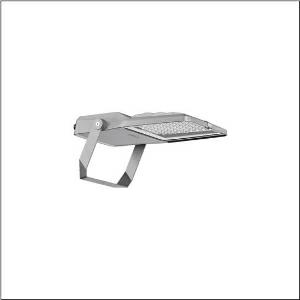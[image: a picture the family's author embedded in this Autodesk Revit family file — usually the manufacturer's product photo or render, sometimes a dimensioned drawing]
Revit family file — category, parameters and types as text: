
# Revit family: floodlight_fl_21_iq_mini___pl64_5xa7772c2e1a_df54
name_source: partatom
category: Lighting Fixtures
units: mm (PartAtom-declared; Revit-internal decimal feet)

## family parameters
Cut with Voids When Loaded = No
Host = Face
Light Source = No
Part Type = Normal
Room Calculation Point = No
Round Connector Dimension = Use Diameter
Shared = No

## types (1)
- --- (1 x LED, 11790 lm, 87.2 W, 3000K)
    Apparent Load = 87 VA
    CIE Flux Codes = 28 80 98 100 100
    Color Rendering = 70
    Color Temperature = 3000K
    Default Elevation = 1800 mm
    Description = Floodlight FL 21 iQ mini, floodlight, primary light control with lens, of PMMA, primary optical cover: protective disc, of toughened safety glass, transparent, light distribution: PL64, light emission: direct distribution, installation type: surface-mounted, lamps: LED, High Power LED, rated values: 11.790lm | 87,2W | 135,2lm/W (begin service life); end service life: 11.790lm | 92,1W; at 50% lumin. flux: 5.895lm | 40,1W | 147lm/W, colour temperature: 3000K, colour rendering: CRI > 70, light colour: 730, light setting 1 begin service life: 100% | 11.790lm | 87,2W | 135,2lm/W | 3.000K, light setting 1 end service life: 92,1W, further light settings possible, control: Street-Remote, Auto-Match, Temp-Guard, Night-Set, Smart-Wire, Desk-Remote (wireless, voltage-free reading and setting of iQ features in the workshop via application-optimized NFC function/RFID function), optimised constant luminous flux control (CLO 2.0), pre-setting: linear dimming characteristic, with terminal, 6-pole, mains connection: 220..240V, AC, 50/60Hz, luminaire housing, of diecast aluminium, powder-coated, SITECO metallic grey (DB 702S), corrosivity category C5 mid according to DIN EN ISO 12944suitable for swimming poolschlorine-resistant, sealing non-destructively replaceable, mounting bracket, of steel, galvanised, powder-coated, SITECO metallic grey (DB 702S), protection rating (complete): IP66, insulation class (complete): insulation class II (safety insulation), certification: CE, ENEC, VDE, protection symbol: D, impact resistance: IK08, permissible operating ambient temperature: -40..+40°C, permissible operating ambient temperature for outdoor applications: -40..+50°C, standard: DIN EN 12944, LABS conformity tested according to VDMA 24364:2018-05, packaging unit: 1 piece

Light Distribution: PL64
    Height = 70 mm
    Lamp = 1 x LED
    Lamp Light Flux = 11790 lm
    Lamp Power = 87.2 W
    Lamp count = 1
    Length = 485 mm
    Luminous efficacy = 135 lm/W
    Manufacturer = Siteco
    ModVariant = No
    Model = 5XA7772C2E1A
    Number of Poles = 1
    OnlyDefault = Yes
    Power Factor = 1
    Product Name = Floodlight FL 21 iQ mini | PL64
    Product group = floodlight | pylon annexe
    ProductGroupID = 6201
    Protection Class = Protection class II
    Protection Degree = IP 66
    RLX_Detail_Level = 1
    RLX_Emergency_Light_Flux = 0 lm
    RLX_Emergency_Type = 0
    RLX_Emergency_Type_DB = No
    RlxData = <blob elided: 96669 chars, md5=c1a87658>
    Socket = socket
    Standby Power = 0 W
    System Light Flux = 11790 lm
    System Power = 87 W
    Type Comments = factory setting: luminous flux: 100 % | dim-lin: 254 | 456 mA
    Type Image = l_1006845.jpg
    URL = http://relux.com
    VarID = @adj_165911
    Voltage = 0 V
    Weight = 0.00 kg
    Width = 337 mm

## geometry (parser evidence)
native form markers: Blend x4, Sweep x12
no freeform markers — native parametric forms only
